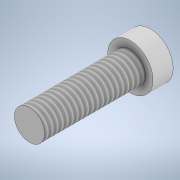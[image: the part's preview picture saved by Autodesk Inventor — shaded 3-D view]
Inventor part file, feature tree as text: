
AUTODESK INVENTOR PART (.ipt)
format: ipt  version: 2020 (Build 240168000, 168)  size: 109,056 bytes
history: native  units: in
note: dims shown in document units (in); Inventor stores cm internally (conversion verified against a paired STEP export)
features: sketch x2, extrude x2, thread x1
ambient origin geometry x8: Origin, YZ Plane, XZ Plane, XY Plane, X Axis, Y Axis, Z Axis, Center Point
bodies: Solid1 (feature_tree)
feature tree (5):
  sketch  "Sketch1"  dims[d0=0.1181in d1=0.1772in]
  extrude  "Extrusion1"  Depth=0.1772in
  extrude  "Extrusion2"  Depth=0.3937in TaperAngle=0.0deg
  thread  "Thread1"  [1 undecoded]
  sketch  "Sketch2"  dims[d2=0.1181in d3=0.1772in d4=0.3937in d5=0.0in d6=0.0787in d7=0.0in d8=0.3937in d9=0.0in]
note: 1 required parameter value undecoded (feature->parameter linkage not recoverable at this tier; creation-order binding heuristic only, values carry confidence <= 0.55)
